# Revit family: Haworth_JiveTable_Rectangle_Bases
name_source: partatom
category: Furniture Systems
revit_build: Autodesk Revit 2018 (Build: 20170223_1515(x64)
units: mm (PartAtom-declared; Revit-internal decimal feet)

## family parameters
Always vertical = Yes
Cut with Voids When Loaded = No
OmniClass Number = 23.40.70.14.64.21
OmniClass Title = Systems Furniture
Part Type = Normal
Room Calculation Point = No
Round Connector Dimension = Use Diameter
Shared = No
Work Plane-Based = No

## types (77) — shared parameters
Assembly Code = E2020200
Manufacturer = Haworth, Inc.
Max. Depth = 60"
Max. Height = 42"
Max. Width = 216"
Min. Depth = 24"
Min. Height = 16"
Min. Width = 24"
Model = Haworth Jive
Revision Number = 0
Size = Verify Final Dim. w/ Haworth
Standard Depths = 24, 30, 36, 42, 48, 54, 60in.
Standard Heights = 16, 20, 29, 36, 42 in.
Standard Widths = 24, 30, 36, 42, 48, 54, 60, 72, 84, 96, 108, 120, 144, 180, 216 in.
Table Thickness = 1 3/16"
URL = https://www.haworth.com
URL - Product = http://www.haworth.com
Warranty = http://www.haworth.com

## per-type parameters (varying)
- 30d 30w 29h - X Base - With Casters: 2 Column=No; 3 Column=No; 4 6 8 Column=No; 4 Column=No; 4 Column at 48d 48w=No; 6 Column=No; 8 Column=No; Actual Casters=Yes; Actual Depth=30"; Actual Glide=No; Actual Height=29"; Actual Table Depth=48"; Actual Table Width=48"; Actual Width=30"; Bridge Base 48d 48w Only=No; Bridge Distance=2"; Casters=Yes; Center Leg Location=0"; Columns=No; Custom Size=No; Depth=30"; Description=Haworth Jive Table Rectangle Bases - 30d 30w 29h - X Base - With Casters; Glides=No; Height=29"; Leg Height=27 13/16"; Middle Columns=No; Support Depth 6 8 Column=10 29/32"; Support Distance=0"; Support Distance 6 8 Column=10 29/32"; Width=30"; X Base=Yes; X Base 2 3 Column=Yes; X Base 48d 48w Only=Yes; X Base at 48d 48w=No
- 36d 36w 29h - X Base - With Casters: 2 Column=No; 3 Column=No; 4 6 8 Column=No; 4 Column=No; 4 Column at 48d 48w=No; 6 Column=No; 8 Column=No; Actual Casters=Yes; Actual Depth=36"; Actual Glide=No; Actual Height=29"; Actual Table Depth=48"; Actual Table Width=48"; Actual Width=36"; Bridge Base 48d 48w Only=No; Bridge Distance=2"; Casters=Yes; Center Leg Location=0"; Columns=No; Custom Size=No; Depth=36"; Description=Haworth Jive Table Rectangle Bases - 36d 36w 29h - X Base - With Casters; Glides=No; Height=29"; Leg Height=27 13/16"; Middle Columns=No; Support Depth 6 8 Column=10 29/32"; Support Distance=0"; Support Distance 6 8 Column=10 29/32"; Width=36"; X Base=Yes; X Base 2 3 Column=Yes; X Base 48d 48w Only=Yes; X Base at 48d 48w=No
- 42d 42w 29h - X Base - With Casters: 2 Column=No; 3 Column=No; 4 6 8 Column=No; 4 Column=No; 4 Column at 48d 48w=No; 6 Column=No; 8 Column=No; Actual Casters=Yes; Actual Depth=42"; Actual Glide=No; Actual Height=29"; Actual Table Depth=48"; Actual Table Width=48"; Actual Width=42"; Bridge Base 48d 48w Only=No; Bridge Distance=2"; Casters=Yes; Center Leg Location=0"; Columns=No; Custom Size=No; Depth=42"; Description=Haworth Jive Table Rectangle Bases - 42d 42w 29h - X Base - With Casters; Glides=No; Height=29"; Leg Height=27 13/16"; Middle Columns=No; Support Depth 6 8 Column=10 29/32"; Support Distance=0"; Support Distance 6 8 Column=10 29/32"; Width=42"; X Base=Yes; X Base 2 3 Column=Yes; X Base 48d 48w Only=Yes; X Base at 48d 48w=No
- 48d 48w 29h - X Base - With Casters: 2 Column=No; 3 Column=No; 4 6 8 Column=No; 4 Column=No; 4 Column at 48d 48w=No; 6 Column=No; 8 Column=No; Actual Casters=Yes; Actual Depth=48"; Actual Glide=No; Actual Height=29"; Actual Table Depth=48"; Actual Table Width=48"; Actual Width=48"; Bridge Base 48d 48w Only=No; Bridge Distance=2"; Casters=Yes; Center Leg Location=0"; Columns=No; Custom Size=No; Depth=48"; Description=Haworth Jive Table Rectangle Bases - 48d 48w 29h - X Base - With Casters; Glides=No; Height=29"; Leg Height=27 13/16"; Middle Columns=No; Support Depth 6 8 Column=10 29/32"; Support Distance=0"; Support Distance 6 8 Column=10 29/32"; Width=48"; X Base=Yes; X Base 2 3 Column=Yes; X Base 48d 48w Only=Yes; X Base at 48d 48w=Yes
- 30d 30w 42h - X Base - With Casters: 2 Column=No; 3 Column=No; 4 6 8 Column=No; 4 Column=No; 4 Column at 48d 48w=No; 6 Column=No; 8 Column=No; Actual Casters=Yes; Actual Depth=30"; Actual Glide=No; Actual Height=42"; Actual Table Depth=48"; Actual Table Width=48"; Actual Width=30"; Bridge Base 48d 48w Only=No; Bridge Distance=2"; Casters=Yes; Center Leg Location=0"; Columns=No; Custom Size=No; Depth=30"; Description=Haworth Jive Table Rectangle Bases - 30d 30w 42h - X Base - With Casters; Glides=No; Height=42"; Leg Height=40 13/16"; Middle Columns=No; Support Depth 6 8 Column=10 29/32"; Support Distance=0"; Support Distance 6 8 Column=10 29/32"; Width=30"; X Base=Yes; X Base 2 3 Column=Yes; X Base 48d 48w Only=Yes; X Base at 48d 48w=No
- 36d 36w 42h - X Base - With Casters: 2 Column=No; 3 Column=No; 4 6 8 Column=No; 4 Column=No; 4 Column at 48d 48w=No; 6 Column=No; 8 Column=No; Actual Casters=Yes; Actual Depth=36"; Actual Glide=No; Actual Height=42"; Actual Table Depth=48"; Actual Table Width=48"; Actual Width=36"; Bridge Base 48d 48w Only=No; Bridge Distance=2"; Casters=Yes; Center Leg Location=0"; Columns=No; Custom Size=No; Depth=36"; Description=Haworth Jive Table Rectangle Bases - 36d 36w 42h - X Base - With Casters; Glides=No; Height=42"; Leg Height=40 13/16"; Middle Columns=No; Support Depth 6 8 Column=10 29/32"; Support Distance=0"; Support Distance 6 8 Column=10 29/32"; Width=36"; X Base=Yes; X Base 2 3 Column=Yes; X Base 48d 48w Only=Yes; X Base at 48d 48w=No
- 42d 42w 42h - X Base - With Casters: 2 Column=No; 3 Column=No; 4 6 8 Column=No; 4 Column=No; 4 Column at 48d 48w=No; 6 Column=No; 8 Column=No; Actual Casters=Yes; Actual Depth=42"; Actual Glide=No; Actual Height=42"; Actual Table Depth=48"; Actual Table Width=48"; Actual Width=42"; Bridge Base 48d 48w Only=No; Bridge Distance=2"; Casters=Yes; Center Leg Location=0"; Columns=No; Custom Size=No; Depth=42"; Description=Haworth Jive Table Rectangle Bases - 42d 42w 42h - X Base - With Casters; Glides=No; Height=42"; Leg Height=40 13/16"; Middle Columns=No; Support Depth 6 8 Column=10 29/32"; Support Distance=0"; Support Distance 6 8 Column=10 29/32"; Width=42"; X Base=Yes; X Base 2 3 Column=Yes; X Base 48d 48w Only=Yes; X Base at 48d 48w=No
- 24d 24w 16h - X Base - With Glides: 2 Column=No; 3 Column=No; 4 6 8 Column=No; 4 Column=No; 4 Column at 48d 48w=No; 6 Column=No; 8 Column=No; Actual Casters=No; Actual Depth=24"; Actual Glide=Yes; Actual Height=16"; Actual Table Depth=48"; Actual Table Width=48"; Actual Width=24"; Bridge Base 48d 48w Only=No; Bridge Distance=2"; Casters=No; Center Leg Location=0"; Columns=No; Custom Size=No; Depth=24"; Description=Haworth Jive Table Rectangle Bases - 24d 24w 16h - X Base - With Glides; Glides=Yes; Height=16"; Leg Height=14 13/16"; Middle Columns=No; Support Depth 6 8 Column=10 29/32"; Support Distance=0"; Support Distance 6 8 Column=10 29/32"; Width=24"; X Base=Yes; X Base 2 3 Column=Yes; X Base 48d 48w Only=Yes; X Base at 48d 48w=No
- 30d 30w 16h - X Base - With Glides: 2 Column=No; 3 Column=No; 4 6 8 Column=No; 4 Column=No; 4 Column at 48d 48w=No; 6 Column=No; 8 Column=No; Actual Casters=No; Actual Depth=30"; Actual Glide=Yes; Actual Height=16"; Actual Table Depth=48"; Actual Table Width=48"; Actual Width=30"; Bridge Base 48d 48w Only=No; Bridge Distance=2"; Casters=No; Center Leg Location=0"; Columns=No; Custom Size=No; Depth=30"; Description=Haworth Jive Table Rectangle Bases - 30d 30w 16h - X Base - With Glides; Glides=Yes; Height=16"; Leg Height=14 13/16"; Middle Columns=No; Support Depth 6 8 Column=10 29/32"; Support Distance=0"; Support Distance 6 8 Column=10 29/32"; Width=30"; X Base=Yes; X Base 2 3 Column=Yes; X Base 48d 48w Only=Yes; X Base at 48d 48w=No
- 36d 36w 16h - X Base - With Glides: 2 Column=No; 3 Column=No; 4 6 8 Column=No; 4 Column=No; 4 Column at 48d 48w=No; 6 Column=No; 8 Column=No; Actual Casters=No; Actual Depth=36"; Actual Glide=Yes; Actual Height=16"; Actual Table Depth=48"; Actual Table Width=48"; Actual Width=36"; Bridge Base 48d 48w Only=No; Bridge Distance=2"; Casters=No; Center Leg Location=0"; Columns=No; Custom Size=No; Depth=36"; Description=Haworth Jive Table Rectangle Bases - 36d 36w 16h - X Base - With Glides; Glides=Yes; Height=16"; Leg Height=14 13/16"; Middle Columns=No; Support Depth 6 8 Column=10 29/32"; Support Distance=0"; Support Distance 6 8 Column=10 29/32"; Width=36"; X Base=Yes; X Base 2 3 Column=Yes; X Base 48d 48w Only=Yes; X Base at 48d 48w=No
- 42d 42w 16h - X Base - With Glides: 2 Column=No; 3 Column=No; 4 6 8 Column=No; 4 Column=No; 4 Column at 48d 48w=No; 6 Column=No; 8 Column=No; Actual Casters=No; Actual Depth=42"; Actual Glide=Yes; Actual Height=16"; Actual Table Depth=48"; Actual Table Width=48"; Actual Width=42"; Bridge Base 48d 48w Only=No; Bridge Distance=2"; Casters=No; Center Leg Location=0"; Columns=No; Custom Size=No; Depth=42"; Description=Haworth Jive Table Rectangle Bases - 42d 42w 16h - X Base - With Glides; Glides=Yes; Height=16"; Leg Height=14 13/16"; Middle Columns=No; Support Depth 6 8 Column=10 29/32"; Support Distance=0"; Support Distance 6 8 Column=10 29/32"; Width=42"; X Base=Yes; X Base 2 3 Column=Yes; X Base 48d 48w Only=Yes; X Base at 48d 48w=No
- 48d 48w 16h - X Base - With Glides: 2 Column=No; 3 Column=No; 4 6 8 Column=No; 4 Column=No; 4 Column at 48d 48w=No; 6 Column=No; 8 Column=No; Actual Casters=No; Actual Depth=48"; Actual Glide=Yes; Actual Height=16"; Actual Table Depth=48"; Actual Table Width=48"; Actual Width=48"; Bridge Base 48d 48w Only=No; Bridge Distance=2"; Casters=No; Center Leg Location=0"; Columns=No; Custom Size=No; Depth=48"; Description=Haworth Jive Table Rectangle Bases - 48d 48w 16h - X Base - With Glides; Glides=Yes; Height=16"; Leg Height=14 13/16"; Middle Columns=No; Support Depth 6 8 Column=10 29/32"; Support Distance=0"; Support Distance 6 8 Column=10 29/32"; Width=48"; X Base=Yes; X Base 2 3 Column=Yes; X Base 48d 48w Only=Yes; X Base at 48d 48w=Yes
- 24d 24w 20h - X Base - With Glides: 2 Column=No; 3 Column=No; 4 6 8 Column=No; 4 Column=No; 4 Column at 48d 48w=No; 6 Column=No; 8 Column=No; Actual Casters=No; Actual Depth=24"; Actual Glide=Yes; Actual Height=20"; Actual Table Depth=48"; Actual Table Width=48"; Actual Width=24"; Bridge Base 48d 48w Only=No; Bridge Distance=2"; Casters=No; Center Leg Location=0"; Columns=No; Custom Size=No; Depth=24"; Description=Haworth Jive Table Rectangle Bases - 24d 24w 20h - X Base - With Glides; Glides=Yes; Height=20"; Leg Height=18 13/16"; Middle Columns=No; Support Depth 6 8 Column=10 29/32"; Support Distance=0"; Support Distance 6 8 Column=10 29/32"; Width=24"; X Base=Yes; X Base 2 3 Column=Yes; X Base 48d 48w Only=Yes; X Base at 48d 48w=No
- 30d 30w 20h - X Base - With Glides: 2 Column=No; 3 Column=No; 4 6 8 Column=No; 4 Column=No; 4 Column at 48d 48w=No; 6 Column=No; 8 Column=No; Actual Casters=No; Actual Depth=30"; Actual Glide=Yes; Actual Height=20"; Actual Table Depth=48"; Actual Table Width=48"; Actual Width=30"; Bridge Base 48d 48w Only=No; Bridge Distance=2"; Casters=No; Center Leg Location=0"; Columns=No; Custom Size=No; Depth=30"; Description=Haworth Jive Table Rectangle Bases - 30d 30w 20h - X Base - With Glides; Glides=Yes; Height=20"; Leg Height=18 13/16"; Middle Columns=No; Support Depth 6 8 Column=10 29/32"; Support Distance=0"; Support Distance 6 8 Column=10 29/32"; Width=30"; X Base=Yes; X Base 2 3 Column=Yes; X Base 48d 48w Only=Yes; X Base at 48d 48w=No
- 36d 36w 20h - X Base - With Glides: 2 Column=No; 3 Column=No; 4 6 8 Column=No; 4 Column=No; 4 Column at 48d 48w=No; 6 Column=No; 8 Column=No; Actual Casters=No; Actual Depth=36"; Actual Glide=Yes; Actual Height=20"; Actual Table Depth=48"; Actual Table Width=48"; Actual Width=36"; Bridge Base 48d 48w Only=No; Bridge Distance=2"; Casters=No; Center Leg Location=0"; Columns=No; Custom Size=No; Depth=36"; Description=Haworth Jive Table Rectangle Bases - 36d 36w 20h - X Base - With Glides; Glides=Yes; Height=20"; Leg Height=18 13/16"; Middle Columns=No; Support Depth 6 8 Column=10 29/32"; Support Distance=0"; Support Distance 6 8 Column=10 29/32"; Width=36"; X Base=Yes; X Base 2 3 Column=Yes; X Base 48d 48w Only=Yes; X Base at 48d 48w=No
- 42d 42w 20h - X Base - With Glides: 2 Column=No; 3 Column=No; 4 6 8 Column=No; 4 Column=No; 4 Column at 48d 48w=No; 6 Column=No; 8 Column=No; Actual Casters=No; Actual Depth=42"; Actual Glide=Yes; Actual Height=20"; Actual Table Depth=48"; Actual Table Width=48"; Actual Width=42"; Bridge Base 48d 48w Only=No; Bridge Distance=2"; Casters=No; Center Leg Location=0"; Columns=No; Custom Size=No; Depth=42"; Description=Haworth Jive Table Rectangle Bases - 42d 42w 20h - X Base - With Glides; Glides=Yes; Height=20"; Leg Height=18 13/16"; Middle Columns=No; Support Depth 6 8 Column=10 29/32"; Support Distance=0"; Support Distance 6 8 Column=10 29/32"; Width=42"; X Base=Yes; X Base 2 3 Column=Yes; X Base 48d 48w Only=Yes; X Base at 48d 48w=No
- 48d 48w 20h - X Base - With Glides: 2 Column=No; 3 Column=No; 4 6 8 Column=No; 4 Column=No; 4 Column at 48d 48w=No; 6 Column=No; 8 Column=No; Actual Casters=No; Actual Depth=48"; Actual Glide=Yes; Actual Height=20"; Actual Table Depth=48"; Actual Table Width=48"; Actual Width=48"; Bridge Base 48d 48w Only=No; Bridge Distance=2"; Casters=No; Center Leg Location=0"; Columns=No; Custom Size=No; Depth=48"; Description=Haworth Jive Table Rectangle Bases - 48d 48w 20h - X Base - With Glides; Glides=Yes; Height=20"; Leg Height=18 13/16"; Middle Columns=No; Support Depth 6 8 Column=10 29/32"; Support Distance=0"; Support Distance 6 8 Column=10 29/32"; Width=48"; X Base=Yes; X Base 2 3 Column=Yes; X Base 48d 48w Only=Yes; X Base at 48d 48w=Yes
- 24d 24w 29h - X Base - With Glides: 2 Column=No; 3 Column=No; 4 6 8 Column=No; 4 Column=No; 4 Column at 48d 48w=No; 6 Column=No; 8 Column=No; Actual Casters=No; Actual Depth=24"; Actual Glide=Yes; Actual Height=29"; Actual Table Depth=48"; Actual Table Width=48"; Actual Width=24"; Bridge Base 48d 48w Only=No; Bridge Distance=2"; Casters=No; Center Leg Location=0"; Columns=No; Custom Size=No; Depth=24"; Description=Haworth Jive Table Rectangle Bases - 24d 24w 29h - X Base - With Glides; Glides=Yes; Height=29"; Leg Height=27 13/16"; Middle Columns=No; Support Depth 6 8 Column=10 29/32"; Support Distance=0"; Support Distance 6 8 Column=10 29/32"; Width=24"; X Base=Yes; X Base 2 3 Column=Yes; X Base 48d 48w Only=Yes; X Base at 48d 48w=No
- 30d 30w 29h - X Base - With Glides: 2 Column=No; 3 Column=No; 4 6 8 Column=No; 4 Column=No; 4 Column at 48d 48w=No; 6 Column=No; 8 Column=No; Actual Casters=No; Actual Depth=30"; Actual Glide=Yes; Actual Height=29"; Actual Table Depth=48"; Actual Table Width=48"; Actual Width=30"; Bridge Base 48d 48w Only=No; Bridge Distance=2"; Casters=No; Center Leg Location=0"; Columns=No; Custom Size=No; Depth=30"; Description=Haworth Jive Table Rectangle Bases - 30d 30w 29h - X Base - With Glides; Glides=Yes; Height=29"; Leg Height=27 13/16"; Middle Columns=No; Support Depth 6 8 Column=10 29/32"; Support Distance=0"; Support Distance 6 8 Column=10 29/32"; Width=30"; X Base=Yes; X Base 2 3 Column=Yes; X Base 48d 48w Only=Yes; X Base at 48d 48w=No
- 36d 36w 29h - X Base - With Glides: 2 Column=No; 3 Column=No; 4 6 8 Column=No; 4 Column=No; 4 Column at 48d 48w=No; 6 Column=No; 8 Column=No; Actual Casters=No; Actual Depth=36"; Actual Glide=Yes; Actual Height=29"; Actual Table Depth=48"; Actual Table Width=48"; Actual Width=36"; Bridge Base 48d 48w Only=No; Bridge Distance=2"; Casters=No; Center Leg Location=0"; Columns=No; Custom Size=No; Depth=36"; Description=Haworth Jive Table Rectangle Bases - 36d 36w 29h - X Base - With Glides; Glides=Yes; Height=29"; Leg Height=27 13/16"; Middle Columns=No; Support Depth 6 8 Column=10 29/32"; Support Distance=0"; Support Distance 6 8 Column=10 29/32"; Width=36"; X Base=Yes; X Base 2 3 Column=Yes; X Base 48d 48w Only=Yes; X Base at 48d 48w=No
- 42d 42w 29h - X Base - With Glides: 2 Column=No; 3 Column=No; 4 6 8 Column=No; 4 Column=No; 4 Column at 48d 48w=No; 6 Column=No; 8 Column=No; Actual Casters=No; Actual Depth=42"; Actual Glide=Yes; Actual Height=29"; Actual Table Depth=48"; Actual Table Width=48"; Actual Width=42"; Bridge Base 48d 48w Only=No; Bridge Distance=2"; Casters=No; Center Leg Location=0"; Columns=No; Custom Size=No; Depth=42"; Description=Haworth Jive Table Rectangle Bases - 42d 42w 29h - X Base - With Glides; Glides=Yes; Height=29"; Leg Height=27 13/16"; Middle Columns=No; Support Depth 6 8 Column=10 29/32"; Support Distance=0"; Support Distance 6 8 Column=10 29/32"; Width=42"; X Base=Yes; X Base 2 3 Column=Yes; X Base 48d 48w Only=Yes; X Base at 48d 48w=No
- 48d 48w 29h - X Base - With Glides: 2 Column=No; 3 Column=No; 4 6 8 Column=No; 4 Column=No; 4 Column at 48d 48w=No; 6 Column=No; 8 Column=No; Actual Casters=No; Actual Depth=48"; Actual Glide=Yes; Actual Height=29"; Actual Table Depth=48"; Actual Table Width=48"; Actual Width=48"; Bridge Base 48d 48w Only=No; Bridge Distance=2"; Casters=No; Center Leg Location=0"; Columns=No; Custom Size=No; Depth=48"; Description=Haworth Jive Table Rectangle Bases - 48d 48w 29h - X Base - With Glides; Glides=Yes; Height=29"; Leg Height=27 13/16"; Middle Columns=No; Support Depth 6 8 Column=10 29/32"; Support Distance=0"; Support Distance 6 8 Column=10 29/32"; Width=48"; X Base=Yes; X Base 2 3 Column=Yes; X Base 48d 48w Only=Yes; X Base at 48d 48w=Yes
- 30d 30w 36h - X Base - With Glides: 2 Column=No; 3 Column=No; 4 6 8 Column=No; 4 Column=No; 4 Column at 48d 48w=No; 6 Column=No; 8 Column=No; Actual Casters=No; Actual Depth=30"; Actual Glide=Yes; Actual Height=36"; Actual Table Depth=48"; Actual Table Width=48"; Actual Width=30"; Bridge Base 48d 48w Only=No; Bridge Distance=2"; Casters=No; Center Leg Location=0"; Columns=No; Custom Size=No; Depth=30"; Description=Haworth Jive Table Rectangle Bases - 30d 30w 36h - X Base - With Glides; Glides=Yes; Height=36"; Leg Height=34 13/16"; Middle Columns=No; Support Depth 6 8 Column=10 29/32"; Support Distance=0"; Support Distance 6 8 Column=10 29/32"; Width=30"; X Base=Yes; X Base 2 3 Column=Yes; X Base 48d 48w Only=Yes; X Base at 48d 48w=No
- 36d 36w 36h - X Base - With Glides: 2 Column=No; 3 Column=No; 4 6 8 Column=No; 4 Column=No; 4 Column at 48d 48w=No; 6 Column=No; 8 Column=No; Actual Casters=No; Actual Depth=36"; Actual Glide=Yes; Actual Height=36"; Actual Table Depth=48"; Actual Table Width=48"; Actual Width=36"; Bridge Base 48d 48w Only=No; Bridge Distance=2"; Casters=No; Center Leg Location=0"; Columns=No; Custom Size=No; Depth=36"; Description=Haworth Jive Table Rectangle Bases - 36d 36w 36h - X Base - With Glides; Glides=Yes; Height=36"; Leg Height=34 13/16"; Middle Columns=No; Support Depth 6 8 Column=10 29/32"; Support Distance=0"; Support Distance 6 8 Column=10 29/32"; Width=36"; X Base=Yes; X Base 2 3 Column=Yes; X Base 48d 48w Only=Yes; X Base at 48d 48w=No
- 42d 42w 36h - X Base - With Glides: 2 Column=No; 3 Column=No; 4 6 8 Column=No; 4 Column=No; 4 Column at 48d 48w=No; 6 Column=No; 8 Column=No; Actual Casters=No; Actual Depth=42"; Actual Glide=Yes; Actual Height=36"; Actual Table Depth=48"; Actual Table Width=48"; Actual Width=42"; Bridge Base 48d 48w Only=No; Bridge Distance=2"; Casters=No; Center Leg Location=0"; Columns=No; Custom Size=No; Depth=42"; Description=Haworth Jive Table Rectangle Bases - 42d 42w 36h - X Base - With Glides; Glides=Yes; Height=36"; Leg Height=34 13/16"; Middle Columns=No; Support Depth 6 8 Column=10 29/32"; Support Distance=0"; Support Distance 6 8 Column=10 29/32"; Width=42"; X Base=Yes; X Base 2 3 Column=Yes; X Base 48d 48w Only=Yes; X Base at 48d 48w=No
- 30d 30w 42h - X Base - With Glides: 2 Column=No; 3 Column=No; 4 6 8 Column=No; 4 Column=No; 4 Column at 48d 48w=No; 6 Column=No; 8 Column=No; Actual Casters=No; Actual Depth=30"; Actual Glide=Yes; Actual Height=42"; Actual Table Depth=48"; Actual Table Width=48"; Actual Width=30"; Bridge Base 48d 48w Only=No; Bridge Distance=2"; Casters=No; Center Leg Location=0"; Columns=No; Custom Size=No; Depth=30"; Description=Haworth Jive Table Rectangle Bases - 30d 30w 42h - X Base - With Glides; Glides=Yes; Height=42"; Leg Height=40 13/16"; Middle Columns=No; Support Depth 6 8 Column=10 29/32"; Support Distance=0"; Support Distance 6 8 Column=10 29/32"; Width=30"; X Base=Yes; X Base 2 3 Column=Yes; X Base 48d 48w Only=Yes; X Base at 48d 48w=No
- 36d 36w 42h - X Base - With Glides: 2 Column=No; 3 Column=No; 4 6 8 Column=No; 4 Column=No; 4 Column at 48d 48w=No; 6 Column=No; 8 Column=No; Actual Casters=No; Actual Depth=36"; Actual Glide=Yes; Actual Height=42"; Actual Table Depth=48"; Actual Table Width=48"; Actual Width=36"; Bridge Base 48d 48w Only=No; Bridge Distance=2"; Casters=No; Center Leg Location=0"; Columns=No; Custom Size=No; Depth=36"; Description=Haworth Jive Table Rectangle Bases - 36d 36w 42h - X Base - With Glides; Glides=Yes; Height=42"; Leg Height=40 13/16"; Middle Columns=No; Support Depth 6 8 Column=10 29/32"; Support Distance=0"; Support Distance 6 8 Column=10 29/32"; Width=36"; X Base=Yes; X Base 2 3 Column=Yes; X Base 48d 48w Only=Yes; X Base at 48d 48w=No
- 42d 42w 42h - X Base - With Glides: 2 Column=No; 3 Column=No; 4 6 8 Column=No; 4 Column=No; 4 Column at 48d 48w=No; 6 Column=No; 8 Column=No; Actual Casters=No; Actual Depth=42"; Actual Glide=Yes; Actual Height=42"; Actual Table Depth=48"; Actual Table Width=48"; Actual Width=42"; Bridge Base 48d 48w Only=No; Bridge Distance=2"; Casters=No; Center Leg Location=0"; Columns=No; Custom Size=No; Depth=42"; Description=Haworth Jive Table Rectangle Bases - 42d 42w 42h - X Base - With Glides; Glides=Yes; Height=42"; Leg Height=40 13/16"; Middle Columns=No; Support Depth 6 8 Column=10 29/32"; Support Distance=0"; Support Distance 6 8 Column=10 29/32"; Width=42"; X Base=Yes; X Base 2 3 Column=Yes; X Base 48d 48w Only=Yes; X Base at 48d 48w=No
- 48d 48w 29h - Bridge Base - With Glides: 2 Column=No; 3 Column=No; 4 6 8 Column=Yes; 4 Column=Yes; 4 Column at 48d 48w=Yes; 6 Column=No; 8 Column=No; Actual Casters=No; Actual Depth=48"; Actual Glide=Yes; Actual Height=29"; Actual Table Depth=48"; Actual Table Width=48"; Actual Width=48"; Bridge Base 48d 48w Only=Yes; Bridge Distance=24"; Casters=No; Center Leg Location=0"; Columns=No; Custom Size=No; Depth=48"; Description=Haworth Jive Table Rectangle Bases - 48d 48w 29h - Bridge Base - With Glides; Glides=Yes; Height=29"; Leg Height=27 13/16"; Middle Columns=No; Support Depth 6 8 Column=10 29/32"; Support Distance=26"; Support Distance 6 8 Column=10 29/32"; Width=48"; X Base=No; X Base 2 3 Column=No; X Base 48d 48w Only=No; X Base at 48d 48w=No
- 54d 54w 29h - Bridge Base - With Glides: 2 Column=No; 3 Column=No; 4 6 8 Column=Yes; 4 Column=Yes; 4 Column at 48d 48w=No; 6 Column=No; 8 Column=No; Actual Casters=No; Actual Depth=54"; Actual Glide=Yes; Actual Height=29"; Actual Table Depth=54"; Actual Table Width=54"; Actual Width=54"; Bridge Base 48d 48w Only=No; Bridge Distance=24"; Casters=No; Center Leg Location=0"; Columns=No; Custom Size=No; Depth=54"; Description=Haworth Jive Table Rectangle Bases - 54d 54w 29h - Bridge Base - With Glides; Glides=Yes; Height=29"; Leg Height=27 13/16"; Middle Columns=No; Support Depth 6 8 Column=16 29/32"; Support Distance=26"; Support Distance 6 8 Column=16 29/32"; Width=54"; X Base=No; X Base 2 3 Column=No; X Base 48d 48w Only=Yes; X Base at 48d 48w=No
- 60d 60w 29h - Bridge Base - With Glides: 2 Column=No; 3 Column=No; 4 6 8 Column=Yes; 4 Column=Yes; 4 Column at 48d 48w=No; 6 Column=No; 8 Column=No; Actual Casters=No; Actual Depth=60"; Actual Glide=Yes; Actual Height=29"; Actual Table Depth=60"; Actual Table Width=60"; Actual Width=60"; Bridge Base 48d 48w Only=No; Bridge Distance=24"; Casters=No; Center Leg Location=0"; Columns=No; Custom Size=No; Depth=60"; Description=Haworth Jive Table Rectangle Bases - 60d 60w 29h - Bridge Base - With Glides; Glides=Yes; Height=29"; Leg Height=27 13/16"; Middle Columns=No; Support Depth 6 8 Column=14 17/64"; Support Distance=26"; Support Distance 6 8 Column=14 17/64"; Width=60"; X Base=No; X Base 2 3 Column=No; X Base 48d 48w Only=Yes; X Base at 48d 48w=No
- 30d 48w 16h - Bridge Base - With Glides: 2 Column=No; 3 Column=No; 4 6 8 Column=Yes; 4 Column=No; 4 Column at 48d 48w=No; 6 Column=No; 8 Column=No; Actual Casters=No; Actual Depth=30"; Actual Glide=Yes; Actual Height=16"; Actual Table Depth=48"; Actual Table Width=48"; Actual Width=48"; Bridge Base 48d 48w Only=No; Bridge Distance=24"; Casters=No; Center Leg Location=0"; Columns=No; Custom Size=No; Depth=30"; Description=Haworth Jive Table Rectangle Bases - 30d 48w 16h - Bridge Base - With Glides; Glides=Yes; Height=16"; Leg Height=14 13/16"; Middle Columns=No; Support Depth 6 8 Column=10 29/32"; Support Distance=26"; Support Distance 6 8 Column=10 29/32"; Width=48"; X Base=No; X Base 2 3 Column=No; X Base 48d 48w Only=Yes; X Base at 48d 48w=No
- 30d 60w 16h - Bridge Base - With Glides: 2 Column=Yes; 3 Column=No; 4 6 8 Column=No; 4 Column=No; 4 Column at 48d 48w=No; 6 Column=No; 8 Column=No; Actual Casters=No; Actual Depth=30"; Actual Glide=Yes; Actual Height=16"; Actual Table Depth=48"; Actual Table Width=60"; Actual Width=60"; Bridge Base 48d 48w Only=No; Bridge Distance=12"; Casters=No; Center Leg Location=0"; Columns=Yes; Custom Size=No; Depth=30"; Description=Haworth Jive Table Rectangle Bases - 30d 60w 16h - Bridge Base - With Glides; Glides=Yes; Height=16"; Leg Height=14 13/16"; Middle Columns=No; Support Depth 6 8 Column=10 29/32"; Support Distance=14"; Support Distance 6 8 Column=22 29/32"; Width=60"; X Base=No; X Base 2 3 Column=Yes; X Base 48d 48w Only=Yes; X Base at 48d 48w=No
- 30d 72w 16h - Bridge Base - With Glides: 2 Column=Yes; 3 Column=No; 4 6 8 Column=No; 4 Column=No; 4 Column at 48d 48w=No; 6 Column=No; 8 Column=No; Actual Casters=No; Actual Depth=30"; Actual Glide=Yes; Actual Height=16"; Actual Table Depth=48"; Actual Table Width=72"; Actual Width=72"; Bridge Base 48d 48w Only=No; Bridge Distance=24"; Casters=No; Center Leg Location=0"; Columns=Yes; Custom Size=No; Depth=30"; Description=Haworth Jive Table Rectangle Bases - 30d 72w 16h - Bridge Base - With Glides; Glides=Yes; Height=16"; Leg Height=14 13/16"; Middle Columns=No; Support Depth 6 8 Column=10 29/32"; Support Distance=26"; Support Distance 6 8 Column=34 29/32"; Width=72"; X Base=No; X Base 2 3 Column=Yes; X Base 48d 48w Only=Yes; X Base at 48d 48w=No
- 36d 60w 16h - Bridge Base - With Glides: 2 Column=Yes; 3 Column=No; 4 6 8 Column=No; 4 Column=No; 4 Column at 48d 48w=No; 6 Column=No; 8 Column=No; Actual Casters=No; Actual Depth=36"; Actual Glide=Yes; Actual Height=16"; Actual Table Depth=48"; Actual Table Width=60"; Actual Width=60"; Bridge Base 48d 48w Only=No; Bridge Distance=12"; Casters=No; Center Leg Location=0"; Columns=Yes; Custom Size=No; Depth=36"; Description=Haworth Jive Table Rectangle Bases - 36d 60w 16h - Bridge Base - With Glides; Glides=Yes; Height=16"; Leg Height=14 13/16"; Middle Columns=No; Support Depth 6 8 Column=10 29/32"; Support Distance=14"; Support Distance 6 8 Column=22 29/32"; Width=60"; X Base=No; X Base 2 3 Column=Yes; X Base 48d 48w Only=Yes; X Base at 48d 48w=No
- 36d 72w 16h - Bridge Base - With Glides: 2 Column=Yes; 3 Column=No; 4 6 8 Column=No; 4 Column=No; 4 Column at 48d 48w=No; 6 Column=No; 8 Column=No; Actual Casters=No; Actual Depth=36"; Actual Glide=Yes; Actual Height=16"; Actual Table Depth=48"; Actual Table Width=72"; Actual Width=72"; Bridge Base 48d 48w Only=No; Bridge Distance=24"; Casters=No; Center Leg Location=0"; Columns=Yes; Custom Size=No; Depth=36"; Description=Haworth Jive Table Rectangle Bases - 36d 72w 16h - Bridge Base - With Glides; Glides=Yes; Height=16"; Leg Height=14 13/16"; Middle Columns=No; Support Depth 6 8 Column=10 29/32"; Support Distance=26"; Support Distance 6 8 Column=34 29/32"; Width=72"; X Base=No; X Base 2 3 Column=Yes; X Base 48d 48w Only=Yes; X Base at 48d 48w=No
- 30d 48w 20h - Bridge Base - With Glides: 2 Column=No; 3 Column=No; 4 6 8 Column=Yes; 4 Column=No; 4 Column at 48d 48w=No; 6 Column=No; 8 Column=No; Actual Casters=No; Actual Depth=30"; Actual Glide=Yes; Actual Height=20"; Actual Table Depth=48"; Actual Table Width=48"; Actual Width=48"; Bridge Base 48d 48w Only=No; Bridge Distance=24"; Casters=No; Center Leg Location=0"; Columns=No; Custom Size=No; Depth=30"; Description=Haworth Jive Table Rectangle Bases - 30d 48w 20h - Bridge Base - With Glides; Glides=Yes; Height=20"; Leg Height=18 13/16"; Middle Columns=No; Support Depth 6 8 Column=10 29/32"; Support Distance=26"; Support Distance 6 8 Column=10 29/32"; Width=48"; X Base=No; X Base 2 3 Column=No; X Base 48d 48w Only=Yes; X Base at 48d 48w=No
- 30d 60w 20h - Bridge Base - With Glides: 2 Column=Yes; 3 Column=No; 4 6 8 Column=No; 4 Column=No; 4 Column at 48d 48w=No; 6 Column=No; 8 Column=No; Actual Casters=No; Actual Depth=30"; Actual Glide=Yes; Actual Height=20"; Actual Table Depth=48"; Actual Table Width=60"; Actual Width=60"; Bridge Base 48d 48w Only=No; Bridge Distance=12"; Casters=No; Center Leg Location=0"; Columns=Yes; Custom Size=No; Depth=30"; Description=Haworth Jive Table Rectangle Bases - 30d 60w 20h - Bridge Base - With Glides; Glides=Yes; Height=20"; Leg Height=18 13/16"; Middle Columns=No; Support Depth 6 8 Column=10 29/32"; Support Distance=14"; Support Distance 6 8 Column=22 29/32"; Width=60"; X Base=No; X Base 2 3 Column=Yes; X Base 48d 48w Only=Yes; X Base at 48d 48w=No
- 30d 72w 20h - Bridge Base - With Glides: 2 Column=Yes; 3 Column=No; 4 6 8 Column=No; 4 Column=No; 4 Column at 48d 48w=No; 6 Column=No; 8 Column=No; Actual Casters=No; Actual Depth=30"; Actual Glide=Yes; Actual Height=20"; Actual Table Depth=48"; Actual Table Width=72"; Actual Width=72"; Bridge Base 48d 48w Only=No; Bridge Distance=24"; Casters=No; Center Leg Location=0"; Columns=Yes; Custom Size=No; Depth=30"; Description=Haworth Jive Table Rectangle Bases - 30d 72w 20h - Bridge Base - With Glides; Glides=Yes; Height=20"; Leg Height=18 13/16"; Middle Columns=No; Support Depth 6 8 Column=10 29/32"; Support Distance=26"; Support Distance 6 8 Column=34 29/32"; Width=72"; X Base=No; X Base 2 3 Column=Yes; X Base 48d 48w Only=Yes; X Base at 48d 48w=No
- 36d 60w 20h - Bridge Base - With Glides: 2 Column=Yes; 3 Column=No; 4 6 8 Column=No; 4 Column=No; 4 Column at 48d 48w=No; 6 Column=No; 8 Column=No; Actual Casters=No; Actual Depth=36"; Actual Glide=Yes; Actual Height=20"; Actual Table Depth=48"; Actual Table Width=60"; Actual Width=60"; Bridge Base 48d 48w Only=No; Bridge Distance=12"; Casters=No; Center Leg Location=0"; Columns=Yes; Custom Size=No; Depth=36"; Description=Haworth Jive Table Rectangle Bases - 36d 60w 20h - Bridge Base - With Glides; Glides=Yes; Height=20"; Leg Height=18 13/16"; Middle Columns=No; Support Depth 6 8 Column=10 29/32"; Support Distance=14"; Support Distance 6 8 Column=22 29/32"; Width=60"; X Base=No; X Base 2 3 Column=Yes; X Base 48d 48w Only=Yes; X Base at 48d 48w=No
- 36d 72w 20h - Bridge Base - With Glides: 2 Column=Yes; 3 Column=No; 4 6 8 Column=No; 4 Column=No; 4 Column at 48d 48w=No; 6 Column=No; 8 Column=No; Actual Casters=No; Actual Depth=36"; Actual Glide=Yes; Actual Height=20"; Actual Table Depth=48"; Actual Table Width=72"; Actual Width=72"; Bridge Base 48d 48w Only=No; Bridge Distance=24"; Casters=No; Center Leg Location=0"; Columns=Yes; Custom Size=No; Depth=36"; Description=Haworth Jive Table Rectangle Bases - 36d 72w 20h - Bridge Base - With Glides; Glides=Yes; Height=20"; Leg Height=18 13/16"; Middle Columns=No; Support Depth 6 8 Column=10 29/32"; Support Distance=26"; Support Distance 6 8 Column=34 29/32"; Width=72"; X Base=No; X Base 2 3 Column=Yes; X Base 48d 48w Only=Yes; X Base at 48d 48w=No
- 30d 48w 29h - Bridge Base - With Glides: 2 Column=No; 3 Column=No; 4 6 8 Column=Yes; 4 Column=No; 4 Column at 48d 48w=No; 6 Column=No; 8 Column=No; Actual Casters=No; Actual Depth=30"; Actual Glide=Yes; Actual Height=29"; Actual Table Depth=48"; Actual Table Width=48"; Actual Width=48"; Bridge Base 48d 48w Only=No; Bridge Distance=24"; Casters=No; Center Leg Location=0"; Columns=No; Custom Size=No; Depth=30"; Description=Haworth Jive Table Rectangle Bases - 30d 48w 29h - Bridge Base - With Glides; Glides=Yes; Height=29"; Leg Height=27 13/16"; Middle Columns=No; Support Depth 6 8 Column=10 29/32"; Support Distance=26"; Support Distance 6 8 Column=10 29/32"; Width=48"; X Base=No; X Base 2 3 Column=No; X Base 48d 48w Only=Yes; X Base at 48d 48w=No
- 30d 60w 29h - Bridge Base - With Glides: 2 Column=Yes; 3 Column=No; 4 6 8 Column=No; 4 Column=No; 4 Column at 48d 48w=No; 6 Column=No; 8 Column=No; Actual Casters=No; Actual Depth=30"; Actual Glide=Yes; Actual Height=29"; Actual Table Depth=48"; Actual Table Width=60"; Actual Width=60"; Bridge Base 48d 48w Only=No; Bridge Distance=12"; Casters=No; Center Leg Location=0"; Columns=Yes; Custom Size=No; Depth=30"; Description=Haworth Jive Table Rectangle Bases - 30d 60w 29h - Bridge Base - With Glides; Glides=Yes; Height=29"; Leg Height=27 13/16"; Middle Columns=No; Support Depth 6 8 Column=10 29/32"; Support Distance=14"; Support Distance 6 8 Column=22 29/32"; Width=60"; X Base=No; X Base 2 3 Column=Yes; X Base 48d 48w Only=Yes; X Base at 48d 48w=No
- 30d 72w 29h - Bridge Base - With Glides: 2 Column=Yes; 3 Column=No; 4 6 8 Column=No; 4 Column=No; 4 Column at 48d 48w=No; 6 Column=No; 8 Column=No; Actual Casters=No; Actual Depth=30"; Actual Glide=Yes; Actual Height=29"; Actual Table Depth=48"; Actual Table Width=72"; Actual Width=72"; Bridge Base 48d 48w Only=No; Bridge Distance=24"; Casters=No; Center Leg Location=0"; Columns=Yes; Custom Size=No; Depth=30"; Description=Haworth Jive Table Rectangle Bases - 30d 72w 29h - Bridge Base - With Glides; Glides=Yes; Height=29"; Leg Height=27 13/16"; Middle Columns=No; Support Depth 6 8 Column=10 29/32"; Support Distance=26"; Support Distance 6 8 Column=34 29/32"; Width=72"; X Base=No; X Base 2 3 Column=Yes; X Base 48d 48w Only=Yes; X Base at 48d 48w=No
- 36d 60w 29h - Bridge Base - With Glides: 2 Column=Yes; 3 Column=No; 4 6 8 Column=No; 4 Column=No; 4 Column at 48d 48w=No; 6 Column=No; 8 Column=No; Actual Casters=No; Actual Depth=36"; Actual Glide=Yes; Actual Height=29"; Actual Table Depth=48"; Actual Table Width=60"; Actual Width=60"; Bridge Base 48d 48w Only=No; Bridge Distance=12"; Casters=No; Center Leg Location=0"; Columns=Yes; Custom Size=No; Depth=36"; Description=Haworth Jive Table Rectangle Bases - 36d 60w 29h - Bridge Base - With Glides; Glides=Yes; Height=29"; Leg Height=27 13/16"; Middle Columns=No; Support Depth 6 8 Column=10 29/32"; Support Distance=14"; Support Distance 6 8 Column=22 29/32"; Width=60"; X Base=No; X Base 2 3 Column=Yes; X Base 48d 48w Only=Yes; X Base at 48d 48w=No
- 36d 72w 29h - Bridge Base - With Glides: 2 Column=Yes; 3 Column=No; 4 6 8 Column=No; 4 Column=No; 4 Column at 48d 48w=No; 6 Column=No; 8 Column=No; Actual Casters=No; Actual Depth=36"; Actual Glide=Yes; Actual Height=29"; Actual Table Depth=48"; Actual Table Width=72"; Actual Width=72"; Bridge Base 48d 48w Only=No; Bridge Distance=24"; Casters=No; Center Leg Location=0"; Columns=Yes; Custom Size=No; Depth=36"; Description=Haworth Jive Table Rectangle Bases - 36d 72w 29h - Bridge Base - With Glides; Glides=Yes; Height=29"; Leg Height=27 13/16"; Middle Columns=No; Support Depth 6 8 Column=10 29/32"; Support Distance=26"; Support Distance 6 8 Column=34 29/32"; Width=72"; X Base=No; X Base 2 3 Column=Yes; X Base 48d 48w Only=Yes; X Base at 48d 48w=No
- 42d 84w 29h - Bridge Base - With Glides: 2 Column=No; 3 Column=No; 4 6 8 Column=Yes; 4 Column=No; 4 Column at 48d 48w=No; 6 Column=No; 8 Column=No; Actual Casters=No; Actual Depth=42"; Actual Glide=Yes; Actual Height=29"; Actual Table Depth=48"; Actual Table Width=84"; Actual Width=84"; Bridge Base 48d 48w Only=No; Bridge Distance=24"; Casters=No; Center Leg Location=0"; Columns=No; Custom Size=Yes; Depth=42"; Description=Haworth Jive Table Rectangle Bases - 42d 84w 29h - Bridge Base - With Glides; Glides=Yes; Height=29"; Leg Height=27 13/16"; Middle Columns=No; Support Depth 6 8 Column=10 29/32"; Support Distance=26"; Support Distance 6 8 Column=46 29/32"; Width=84"; X Base=No; X Base 2 3 Column=No; X Base 48d 48w Only=Yes; X Base at 48d 48w=No
- 42d 96w 29h - Bridge Base - With Glides: 2 Column=No; 3 Column=No; 4 6 8 Column=Yes; 4 Column=No; 4 Column at 48d 48w=No; 6 Column=No; 8 Column=No; Actual Casters=No; Actual Depth=42"; Actual Glide=Yes; Actual Height=29"; Actual Table Depth=48"; Actual Table Width=96"; Actual Width=96"; Bridge Base 48d 48w Only=No; Bridge Distance=24"; Casters=No; Center Leg Location=0"; Columns=No; Custom Size=Yes; Depth=42"; Description=Haworth Jive Table Rectangle Bases - 42d 96w 29h - Bridge Base - With Glides; Glides=Yes; Height=29"; Leg Height=27 13/16"; Middle Columns=No; Support Depth 6 8 Column=10 29/32"; Support Distance=26"; Support Distance 6 8 Column=58 29/32"; Width=96"; X Base=No; X Base 2 3 Column=No; X Base 48d 48w Only=Yes; X Base at 48d 48w=No
- 48d 96w 29h - 3 Column - With Glides: 2 Column=No; 3 Column=No; 4 6 8 Column=Yes; 4 Column=No; 4 Column at 48d 48w=No; 6 Column=No; 8 Column=No; Actual Casters=No; Actual Depth=48"; Actual Glide=Yes; Actual Height=29"; Actual Table Depth=48"; Actual Table Width=96"; Actual Width=96"; Bridge Base 48d 48w Only=No; Bridge Distance=24"; Casters=No; Center Leg Location=0"; Columns=No; Custom Size=Yes; Depth=48"; Description=Haworth Jive Table Rectangle Bases - 48d 96w 29h - 3 Column - With Glides; Glides=Yes; Height=29"; Leg Height=27 13/16"; Middle Columns=No; Support Depth 6 8 Column=10 29/32"; Support Distance=26"; Support Distance 6 8 Column=58 29/32"; Width=96"; X Base=No; X Base 2 3 Column=No; X Base 48d 48w Only=Yes; X Base at 48d 48w=No
- 48d 108w 29h - 3 Column - With Glides: 2 Column=No; 3 Column=Yes; 4 6 8 Column=No; 4 Column=No; 4 Column at 48d 48w=No; 6 Column=No; 8 Column=No; Actual Casters=No; Actual Depth=48"; Actual Glide=Yes; Actual Height=29"; Actual Table Depth=48"; Actual Table Width=108"; Actual Width=108"; Bridge Base 48d 48w Only=No; Bridge Distance=60"; Casters=No; Center Leg Location=0"; Columns=Yes; Custom Size=No; Depth=48"; Description=Haworth Jive Table Rectangle Bases - 48d 108w 29h - 3 Column - With Glides; Glides=Yes; Height=29"; Leg Height=27 13/16"; Middle Columns=No; Support Depth 6 8 Column=10 29/32"; Support Distance=62"; Support Distance 6 8 Column=70 29/32"; Width=108"; X Base=No; X Base 2 3 Column=Yes; X Base 48d 48w Only=Yes; X Base at 48d 48w=No
- 48d 120w 29h - 3 Column - With Glides: 2 Column=No; 3 Column=Yes; 4 6 8 Column=No; 4 Column=No; 4 Column at 48d 48w=No; 6 Column=No; 8 Column=No; Actual Casters=No; Actual Depth=48"; Actual Glide=Yes; Actual Height=29"; Actual Table Depth=48"; Actual Table Width=120"; Actual Width=120"; Bridge Base 48d 48w Only=No; Bridge Distance=72"; Casters=No; Center Leg Location=0"; Columns=Yes; Custom Size=No; Depth=48"; Description=Haworth Jive Table Rectangle Bases - 48d 120w 29h - 3 Column - With Glides; Glides=Yes; Height=29"; Leg Height=27 13/16"; Middle Columns=No; Support Depth 6 8 Column=10 29/32"; Support Distance=74"; Support Distance 6 8 Column=82 29/32"; Width=120"; X Base=No; X Base 2 3 Column=Yes; X Base 48d 48w Only=Yes; X Base at 48d 48w=No
- 54d 96w 29h - Bridge Base - With Glides: 2 Column=No; 3 Column=No; 4 6 8 Column=Yes; 4 Column=No; 4 Column at 48d 48w=No; 6 Column=No; 8 Column=No; Actual Casters=No; Actual Depth=54"; Actual Glide=Yes; Actual Height=29"; Actual Table Depth=54"; Actual Table Width=96"; Actual Width=96"; Bridge Base 48d 48w Only=No; Bridge Distance=24"; Casters=No; Center Leg Location=0"; Columns=No; Custom Size=Yes; Depth=54"; Description=Haworth Jive Table Rectangle Bases - 54d 96w 29h - Bridge Base - With Glides; Glides=Yes; Height=29"; Leg Height=27 13/16"; Middle Columns=No; Support Depth 6 8 Column=16 29/32"; Support Distance=26"; Support Distance 6 8 Column=58 29/32"; Width=96"; X Base=No; X Base 2 3 Column=No; X Base 48d 48w Only=Yes; X Base at 48d 48w=No
- 54d 108w 29h - Bridge Base - With Glides: 2 Column=No; 3 Column=No; 4 6 8 Column=Yes; 4 Column=No; 4 Column at 48d 48w=No; 6 Column=Yes; 8 Column=No; Actual Casters=No; Actual Depth=54"; Actual Glide=Yes; Actual Height=29"; Actual Table Depth=54"; Actual Table Width=108"; Actual Width=108"; Bridge Base 48d 48w Only=No; Bridge Distance=24"; Casters=No; Center Leg Location=0"; Columns=No; Custom Size=No; Depth=54"; Description=Haworth Jive Table Rectangle Bases - 54d 108w 29h - Bridge Base - With Glides; Glides=Yes; Height=29"; Leg Height=27 13/16"; Middle Columns=Yes; Support Depth 6 8 Column=16 29/32"; Support Distance=26"; Support Distance 6 8 Column=70 29/32"; Width=108"; X Base=No; X Base 2 3 Column=No; X Base 48d 48w Only=Yes; X Base at 48d 48w=No
- 54d 120w 29h - Bridge Base - With Glides: 2 Column=No; 3 Column=No; 4 6 8 Column=Yes; 4 Column=No; 4 Column at 48d 48w=No; 6 Column=Yes; 8 Column=No; Actual Casters=No; Actual Depth=54"; Actual Glide=Yes; Actual Height=29"; Actual Table Depth=54"; Actual Table Width=120"; Actual Width=120"; Bridge Base 48d 48w Only=No; Bridge Distance=24"; Casters=No; Center Leg Location=0"; Columns=No; Custom Size=No; Depth=54"; Description=Haworth Jive Table Rectangle Bases - 54d 120w 29h - Bridge Base - With Glides; Glides=Yes; Height=29"; Leg Height=27 13/16"; Middle Columns=Yes; Support Depth 6 8 Column=16 29/32"; Support Distance=26"; Support Distance 6 8 Column=82 29/32"; Width=120"; X Base=No; X Base 2 3 Column=No; X Base 48d 48w Only=Yes; X Base at 48d 48w=No
- 54d 144w 29h - Bridge Base - With Glides: 2 Column=No; 3 Column=No; 4 6 8 Column=Yes; 4 Column=No; 4 Column at 48d 48w=No; 6 Column=Yes; 8 Column=No; Actual Casters=No; Actual Depth=54"; Actual Glide=Yes; Actual Height=29"; Actual Table Depth=54"; Actual Table Width=144"; Actual Width=144"; Bridge Base 48d 48w Only=No; Bridge Distance=24"; Casters=No; Center Leg Location=0"; Columns=No; Custom Size=No; Depth=54"; Description=Haworth Jive Table Rectangle Bases - 54d 144w 29h - Bridge Base - With Glides; Glides=Yes; Height=29"; Leg Height=27 13/16"; Middle Columns=Yes; Support Depth 6 8 Column=16 29/32"; Support Distance=26"; Support Distance 6 8 Column=106 29/32"; Width=144"; X Base=No; X Base 2 3 Column=No; X Base 48d 48w Only=Yes; X Base at 48d 48w=No
- 54d 180w 29h - Bridge Base - With Glides: 2 Column=No; 3 Column=No; 4 6 8 Column=Yes; 4 Column=No; 4 Column at 48d 48w=No; 6 Column=No; 8 Column=Yes; Actual Casters=No; Actual Depth=54"; Actual Glide=Yes; Actual Height=29"; Actual Table Depth=54"; Actual Table Width=180"; Actual Width=180"; Bridge Base 48d 48w Only=No; Bridge Distance=24"; Casters=No; Center Leg Location=24"; Columns=No; Custom Size=No; Depth=54"; Description=Haworth Jive Table Rectangle Bases - 54d 180w 29h - Bridge Base - With Glides; Glides=Yes; Height=29"; Leg Height=27 13/16"; Middle Columns=Yes; Support Depth 6 8 Column=16 29/32"; Support Distance=26"; Support Distance 6 8 Column=142 29/32"; Width=180"; X Base=No; X Base 2 3 Column=No; X Base 48d 48w Only=Yes; X Base at 48d 48w=No
- 54d 216w 29h - Bridge Base - With Glides: 2 Column=No; 3 Column=No; 4 6 8 Column=Yes; 4 Column=No; 4 Column at 48d 48w=No; 6 Column=No; 8 Column=Yes; Actual Casters=No; Actual Depth=54"; Actual Glide=Yes; Actual Height=29"; Actual Table Depth=54"; Actual Table Width=216"; Actual Width=216"; Bridge Base 48d 48w Only=No; Bridge Distance=24"; Casters=No; Center Leg Location=33"; Columns=No; Custom Size=No; Depth=54"; Description=Haworth Jive Table Rectangle Bases - 54d 216w 29h - Bridge Base - With Glides; Glides=Yes; Height=29"; Leg Height=27 13/16"; Middle Columns=Yes; Support Depth 6 8 Column=16 29/32"; Support Distance=26"; Support Distance 6 8 Column=178 29/32"; Width=216"; X Base=No; X Base 2 3 Column=No; X Base 48d 48w Only=Yes; X Base at 48d 48w=No
- 30d 48w 36h - Bridge Base - With Glides: 2 Column=No; 3 Column=No; 4 6 8 Column=Yes; 4 Column=No; 4 Column at 48d 48w=No; 6 Column=No; 8 Column=No; Actual Casters=No; Actual Depth=30"; Actual Glide=Yes; Actual Height=36"; Actual Table Depth=48"; Actual Table Width=48"; Actual Width=48"; Bridge Base 48d 48w Only=No; Bridge Distance=24"; Casters=No; Center Leg Location=0"; Columns=No; Custom Size=No; Depth=30"; Description=Haworth Jive Table Rectangle Bases - 30d 48w 36h - Bridge Base - With Glides; Glides=Yes; Height=36"; Leg Height=34 13/16"; Middle Columns=No; Support Depth 6 8 Column=10 29/32"; Support Distance=26"; Support Distance 6 8 Column=10 29/32"; Width=48"; X Base=No; X Base 2 3 Column=No; X Base 48d 48w Only=Yes; X Base at 48d 48w=No
- 30d 60w 36h - Bridge Base - With Glides: 2 Column=Yes; 3 Column=No; 4 6 8 Column=No; 4 Column=No; 4 Column at 48d 48w=No; 6 Column=No; 8 Column=No; Actual Casters=No; Actual Depth=30"; Actual Glide=Yes; Actual Height=36"; Actual Table Depth=48"; Actual Table Width=60"; Actual Width=60"; Bridge Base 48d 48w Only=No; Bridge Distance=12"; Casters=No; Center Leg Location=0"; Columns=Yes; Custom Size=No; Depth=30"; Description=Haworth Jive Table Rectangle Bases - 30d 60w 36h - Bridge Base - With Glides; Glides=Yes; Height=36"; Leg Height=34 13/16"; Middle Columns=No; Support Depth 6 8 Column=10 29/32"; Support Distance=14"; Support Distance 6 8 Column=22 29/32"; Width=60"; X Base=No; X Base 2 3 Column=Yes; X Base 48d 48w Only=Yes; X Base at 48d 48w=No
- 30d 72w 36h - Bridge Base - With Glides: 2 Column=Yes; 3 Column=No; 4 6 8 Column=No; 4 Column=No; 4 Column at 48d 48w=No; 6 Column=No; 8 Column=No; Actual Casters=No; Actual Depth=30"; Actual Glide=Yes; Actual Height=36"; Actual Table Depth=48"; Actual Table Width=72"; Actual Width=72"; Bridge Base 48d 48w Only=No; Bridge Distance=24"; Casters=No; Center Leg Location=0"; Columns=Yes; Custom Size=No; Depth=30"; Description=Haworth Jive Table Rectangle Bases - 30d 72w 36h - Bridge Base - With Glides; Glides=Yes; Height=36"; Leg Height=34 13/16"; Middle Columns=No; Support Depth 6 8 Column=10 29/32"; Support Distance=26"; Support Distance 6 8 Column=34 29/32"; Width=72"; X Base=No; X Base 2 3 Column=Yes; X Base 48d 48w Only=Yes; X Base at 48d 48w=No
- 36d 60w 36h - Bridge Base - With Glides: 2 Column=Yes; 3 Column=No; 4 6 8 Column=No; 4 Column=No; 4 Column at 48d 48w=No; 6 Column=No; 8 Column=No; Actual Casters=No; Actual Depth=36"; Actual Glide=Yes; Actual Height=36"; Actual Table Depth=48"; Actual Table Width=60"; Actual Width=60"; Bridge Base 48d 48w Only=No; Bridge Distance=12"; Casters=No; Center Leg Location=0"; Columns=Yes; Custom Size=No; Depth=36"; Description=Haworth Jive Table Rectangle Bases - 36d 60w 36h - Bridge Base - With Glides; Glides=Yes; Height=36"; Leg Height=34 13/16"; Middle Columns=No; Support Depth 6 8 Column=10 29/32"; Support Distance=14"; Support Distance 6 8 Column=22 29/32"; Width=60"; X Base=No; X Base 2 3 Column=Yes; X Base 48d 48w Only=Yes; X Base at 48d 48w=No
- 36d 72w 36h - Bridge Base - With Glides: 2 Column=Yes; 3 Column=No; 4 6 8 Column=No; 4 Column=No; 4 Column at 48d 48w=No; 6 Column=No; 8 Column=No; Actual Casters=No; Actual Depth=36"; Actual Glide=Yes; Actual Height=36"; Actual Table Depth=48"; Actual Table Width=72"; Actual Width=72"; Bridge Base 48d 48w Only=No; Bridge Distance=24"; Casters=No; Center Leg Location=0"; Columns=Yes; Custom Size=No; Depth=36"; Description=Haworth Jive Table Rectangle Bases - 36d 72w 36h - Bridge Base - With Glides; Glides=Yes; Height=36"; Leg Height=34 13/16"; Middle Columns=No; Support Depth 6 8 Column=10 29/32"; Support Distance=26"; Support Distance 6 8 Column=34 29/32"; Width=72"; X Base=No; X Base 2 3 Column=Yes; X Base 48d 48w Only=Yes; X Base at 48d 48w=No
- 30d 48w 42h - Bridge Base - With Glides: 2 Column=No; 3 Column=No; 4 6 8 Column=Yes; 4 Column=No; 4 Column at 48d 48w=No; 6 Column=No; 8 Column=No; Actual Casters=No; Actual Depth=30"; Actual Glide=Yes; Actual Height=42"; Actual Table Depth=48"; Actual Table Width=48"; Actual Width=48"; Bridge Base 48d 48w Only=No; Bridge Distance=24"; Casters=No; Center Leg Location=0"; Columns=No; Custom Size=No; Depth=30"; Description=Haworth Jive Table Rectangle Bases - 30d 48w 42h - Bridge Base - With Glides; Glides=Yes; Height=42"; Leg Height=40 13/16"; Middle Columns=No; Support Depth 6 8 Column=10 29/32"; Support Distance=26"; Support Distance 6 8 Column=10 29/32"; Width=48"; X Base=No; X Base 2 3 Column=No; X Base 48d 48w Only=Yes; X Base at 48d 48w=No
- 30d 60w 42h - Bridge Base - With Glides: 2 Column=Yes; 3 Column=No; 4 6 8 Column=No; 4 Column=No; 4 Column at 48d 48w=No; 6 Column=No; 8 Column=No; Actual Casters=No; Actual Depth=30"; Actual Glide=Yes; Actual Height=42"; Actual Table Depth=48"; Actual Table Width=60"; Actual Width=60"; Bridge Base 48d 48w Only=No; Bridge Distance=12"; Casters=No; Center Leg Location=0"; Columns=Yes; Custom Size=No; Depth=30"; Description=Haworth Jive Table Rectangle Bases - 30d 60w 42h - Bridge Base - With Glides; Glides=Yes; Height=42"; Leg Height=40 13/16"; Middle Columns=No; Support Depth 6 8 Column=10 29/32"; Support Distance=14"; Support Distance 6 8 Column=22 29/32"; Width=60"; X Base=No; X Base 2 3 Column=Yes; X Base 48d 48w Only=Yes; X Base at 48d 48w=No
- 30d 72w 42h - Bridge Base - With Glides: 2 Column=Yes; 3 Column=No; 4 6 8 Column=No; 4 Column=No; 4 Column at 48d 48w=No; 6 Column=No; 8 Column=No; Actual Casters=No; Actual Depth=30"; Actual Glide=Yes; Actual Height=42"; Actual Table Depth=48"; Actual Table Width=72"; Actual Width=72"; Bridge Base 48d 48w Only=No; Bridge Distance=24"; Casters=No; Center Leg Location=0"; Columns=Yes; Custom Size=No; Depth=30"; Description=Haworth Jive Table Rectangle Bases - 30d 72w 42h - Bridge Base - With Glides; Glides=Yes; Height=42"; Leg Height=40 13/16"; Middle Columns=No; Support Depth 6 8 Column=10 29/32"; Support Distance=26"; Support Distance 6 8 Column=34 29/32"; Width=72"; X Base=No; X Base 2 3 Column=Yes; X Base 48d 48w Only=Yes; X Base at 48d 48w=No
- 36d 60w 42h - Bridge Base - With Glides: 2 Column=Yes; 3 Column=No; 4 6 8 Column=No; 4 Column=No; 4 Column at 48d 48w=No; 6 Column=No; 8 Column=No; Actual Casters=No; Actual Depth=36"; Actual Glide=Yes; Actual Height=42"; Actual Table Depth=48"; Actual Table Width=60"; Actual Width=60"; Bridge Base 48d 48w Only=No; Bridge Distance=12"; Casters=No; Center Leg Location=0"; Columns=Yes; Custom Size=No; Depth=36"; Description=Haworth Jive Table Rectangle Bases - 36d 60w 42h - Bridge Base - With Glides; Glides=Yes; Height=42"; Leg Height=40 13/16"; Middle Columns=No; Support Depth 6 8 Column=10 29/32"; Support Distance=14"; Support Distance 6 8 Column=22 29/32"; Width=60"; X Base=No; X Base 2 3 Column=Yes; X Base 48d 48w Only=Yes; X Base at 48d 48w=No
- 36d 72w 42h - Bridge Base - With Glides: 2 Column=Yes; 3 Column=No; 4 6 8 Column=No; 4 Column=No; 4 Column at 48d 48w=No; 6 Column=No; 8 Column=No; Actual Casters=Yes; Actual Depth=36"; Actual Glide=No; Actual Height=42"; Actual Table Depth=48"; Actual Table Width=72"; Actual Width=72"; Bridge Base 48d 48w Only=No; Bridge Distance=24"; Casters=Yes; Center Leg Location=0"; Columns=Yes; Custom Size=No; Depth=36"; Description=Haworth Jive Table Rectangle Bases - 36d 72w 42h - Bridge Base - With Glides; Glides=No; Height=42"; Leg Height=40 13/16"; Middle Columns=No; Support Depth 6 8 Column=10 29/32"; Support Distance=26"; Support Distance 6 8 Column=34 29/32"; Width=72"; X Base=No; X Base 2 3 Column=Yes; X Base 48d 48w Only=Yes; X Base at 48d 48w=No
- 30d 48w 29h - Bridge Base - With Casters: 2 Column=No; 3 Column=No; 4 6 8 Column=Yes; 4 Column=No; 4 Column at 48d 48w=No; 6 Column=No; 8 Column=No; Actual Casters=Yes; Actual Depth=30"; Actual Glide=No; Actual Height=29"; Actual Table Depth=48"; Actual Table Width=48"; Actual Width=48"; Bridge Base 48d 48w Only=No; Bridge Distance=24"; Casters=Yes; Center Leg Location=0"; Columns=No; Custom Size=No; Depth=30"; Description=Haworth Jive Table Rectangle Bases - 30d 48w 29h - Bridge Base - With Casters; Glides=No; Height=29"; Leg Height=27 13/16"; Middle Columns=No; Support Depth 6 8 Column=10 29/32"; Support Distance=26"; Support Distance 6 8 Column=10 29/32"; Width=48"; X Base=No; X Base 2 3 Column=No; X Base 48d 48w Only=Yes; X Base at 48d 48w=No
- 30d 60w 29h - Bridge Base - With Casters: 2 Column=Yes; 3 Column=No; 4 6 8 Column=No; 4 Column=No; 4 Column at 48d 48w=No; 6 Column=No; 8 Column=No; Actual Casters=Yes; Actual Depth=30"; Actual Glide=No; Actual Height=29"; Actual Table Depth=48"; Actual Table Width=60"; Actual Width=60"; Bridge Base 48d 48w Only=No; Bridge Distance=12"; Casters=Yes; Center Leg Location=0"; Columns=Yes; Custom Size=No; Depth=30"; Description=Haworth Jive Table Rectangle Bases - 30d 60w 29h - Bridge Base - With Casters; Glides=No; Height=29"; Leg Height=27 13/16"; Middle Columns=No; Support Depth 6 8 Column=10 29/32"; Support Distance=14"; Support Distance 6 8 Column=22 29/32"; Width=60"; X Base=No; X Base 2 3 Column=Yes; X Base 48d 48w Only=Yes; X Base at 48d 48w=No
- 30d 72w 29h - Bridge Base - With Casters: 2 Column=Yes; 3 Column=No; 4 6 8 Column=No; 4 Column=No; 4 Column at 48d 48w=No; 6 Column=No; 8 Column=No; Actual Casters=Yes; Actual Depth=30"; Actual Glide=No; Actual Height=29"; Actual Table Depth=48"; Actual Table Width=72"; Actual Width=72"; Bridge Base 48d 48w Only=No; Bridge Distance=24"; Casters=Yes; Center Leg Location=0"; Columns=Yes; Custom Size=No; Depth=30"; Description=Haworth Jive Table Rectangle Bases - 30d 72w 29h - Bridge Base - With Casters; Glides=No; Height=29"; Leg Height=27 13/16"; Middle Columns=No; Support Depth 6 8 Column=10 29/32"; Support Distance=26"; Support Distance 6 8 Column=34 29/32"; Width=72"; X Base=No; X Base 2 3 Column=Yes; X Base 48d 48w Only=Yes; X Base at 48d 48w=No
- 36d 60w 29h - Bridge Base - With Casters: 2 Column=Yes; 3 Column=No; 4 6 8 Column=No; 4 Column=No; 4 Column at 48d 48w=No; 6 Column=No; 8 Column=No; Actual Casters=Yes; Actual Depth=36"; Actual Glide=No; Actual Height=29"; Actual Table Depth=48"; Actual Table Width=60"; Actual Width=60"; Bridge Base 48d 48w Only=No; Bridge Distance=12"; Casters=Yes; Center Leg Location=0"; Columns=Yes; Custom Size=No; Depth=36"; Description=Haworth Jive Table Rectangle Bases - 36d 60w 29h - Bridge Base - With Casters; Glides=No; Height=29"; Leg Height=27 13/16"; Middle Columns=No; Support Depth 6 8 Column=10 29/32"; Support Distance=14"; Support Distance 6 8 Column=22 29/32"; Width=60"; X Base=No; X Base 2 3 Column=Yes; X Base 48d 48w Only=Yes; X Base at 48d 48w=No
- 36d 72w 29h - Bridge Base - With Casters: 2 Column=Yes; 3 Column=No; 4 6 8 Column=No; 4 Column=No; 4 Column at 48d 48w=No; 6 Column=No; 8 Column=No; Actual Casters=Yes; Actual Depth=36"; Actual Glide=No; Actual Height=29"; Actual Table Depth=48"; Actual Table Width=72"; Actual Width=72"; Bridge Base 48d 48w Only=No; Bridge Distance=24"; Casters=Yes; Center Leg Location=0"; Columns=Yes; Custom Size=No; Depth=36"; Description=Haworth Jive Table Rectangle Bases - 36d 72w 29h - Bridge Base - With Casters; Glides=No; Height=29"; Leg Height=27 13/16"; Middle Columns=No; Support Depth 6 8 Column=10 29/32"; Support Distance=26"; Support Distance 6 8 Column=34 29/32"; Width=72"; X Base=No; X Base 2 3 Column=Yes; X Base 48d 48w Only=Yes; X Base at 48d 48w=No
- 30d 48w 42h - Bridge Base - With Casters: 2 Column=No; 3 Column=No; 4 6 8 Column=Yes; 4 Column=No; 4 Column at 48d 48w=No; 6 Column=No; 8 Column=No; Actual Casters=Yes; Actual Depth=30"; Actual Glide=No; Actual Height=42"; Actual Table Depth=48"; Actual Table Width=48"; Actual Width=48"; Bridge Base 48d 48w Only=No; Bridge Distance=24"; Casters=Yes; Center Leg Location=0"; Columns=No; Custom Size=No; Depth=30"; Description=Haworth Jive Table Rectangle Bases - 30d 48w 42h - Bridge Base - With Casters; Glides=No; Height=42"; Leg Height=40 13/16"; Middle Columns=No; Support Depth 6 8 Column=10 29/32"; Support Distance=26"; Support Distance 6 8 Column=10 29/32"; Width=48"; X Base=No; X Base 2 3 Column=No; X Base 48d 48w Only=Yes; X Base at 48d 48w=No
- 30d 60w 42h - Bridge Base - With Casters: 2 Column=Yes; 3 Column=No; 4 6 8 Column=No; 4 Column=No; 4 Column at 48d 48w=No; 6 Column=No; 8 Column=No; Actual Casters=Yes; Actual Depth=30"; Actual Glide=No; Actual Height=42"; Actual Table Depth=48"; Actual Table Width=60"; Actual Width=60"; Bridge Base 48d 48w Only=No; Bridge Distance=12"; Casters=Yes; Center Leg Location=0"; Columns=Yes; Custom Size=No; Depth=30"; Description=Haworth Jive Table Rectangle Bases - 30d 60w 42h - Bridge Base - With Casters; Glides=No; Height=42"; Leg Height=40 13/16"; Middle Columns=No; Support Depth 6 8 Column=10 29/32"; Support Distance=14"; Support Distance 6 8 Column=22 29/32"; Width=60"; X Base=No; X Base 2 3 Column=Yes; X Base 48d 48w Only=Yes; X Base at 48d 48w=No
- 30d 72w 42h - Bridge Base - With Casters: 2 Column=Yes; 3 Column=No; 4 6 8 Column=No; 4 Column=No; 4 Column at 48d 48w=No; 6 Column=No; 8 Column=No; Actual Casters=Yes; Actual Depth=30"; Actual Glide=No; Actual Height=42"; Actual Table Depth=48"; Actual Table Width=72"; Actual Width=72"; Bridge Base 48d 48w Only=No; Bridge Distance=24"; Casters=Yes; Center Leg Location=0"; Columns=Yes; Custom Size=No; Depth=30"; Description=Haworth Jive Table Rectangle Bases - 30d 72w 42h - Bridge Base - With Casters; Glides=No; Height=42"; Leg Height=40 13/16"; Middle Columns=No; Support Depth 6 8 Column=10 29/32"; Support Distance=26"; Support Distance 6 8 Column=34 29/32"; Width=72"; X Base=No; X Base 2 3 Column=Yes; X Base 48d 48w Only=Yes; X Base at 48d 48w=No
- 36d 60w 42h - Bridge Base - With Casters: 2 Column=Yes; 3 Column=No; 4 6 8 Column=No; 4 Column=No; 4 Column at 48d 48w=No; 6 Column=No; 8 Column=No; Actual Casters=Yes; Actual Depth=36"; Actual Glide=No; Actual Height=42"; Actual Table Depth=48"; Actual Table Width=60"; Actual Width=60"; Bridge Base 48d 48w Only=No; Bridge Distance=12"; Casters=Yes; Center Leg Location=0"; Columns=Yes; Custom Size=No; Depth=36"; Description=Haworth Jive Table Rectangle Bases - 36d 60w 42h - Bridge Base - With Casters; Glides=No; Height=42"; Leg Height=40 13/16"; Middle Columns=No; Support Depth 6 8 Column=10 29/32"; Support Distance=14"; Support Distance 6 8 Column=22 29/32"; Width=60"; X Base=No; X Base 2 3 Column=Yes; X Base 48d 48w Only=Yes; X Base at 48d 48w=No
- 36d 72w 42h - Bridge Base - With Casters: 2 Column=Yes; 3 Column=No; 4 6 8 Column=No; 4 Column=No; 4 Column at 48d 48w=No; 6 Column=No; 8 Column=No; Actual Casters=Yes; Actual Depth=36"; Actual Glide=No; Actual Height=42"; Actual Table Depth=48"; Actual Table Width=72"; Actual Width=72"; Bridge Base 48d 48w Only=No; Bridge Distance=24"; Casters=Yes; Center Leg Location=0"; Columns=Yes; Custom Size=No; Depth=36"; Description=Haworth Jive Table Rectangle Bases - 36d 72w 42h - Bridge Base - With Casters; Glides=No; Height=42"; Leg Height=40 13/16"; Middle Columns=No; Support Depth 6 8 Column=10 29/32"; Support Distance=26"; Support Distance 6 8 Column=34 29/32"; Width=72"; X Base=No; X Base 2 3 Column=Yes; X Base 48d 48w Only=Yes; X Base at 48d 48w=No

## geometry (parser evidence)
native form markers: Sweep x26
no freeform markers — native parametric forms only
